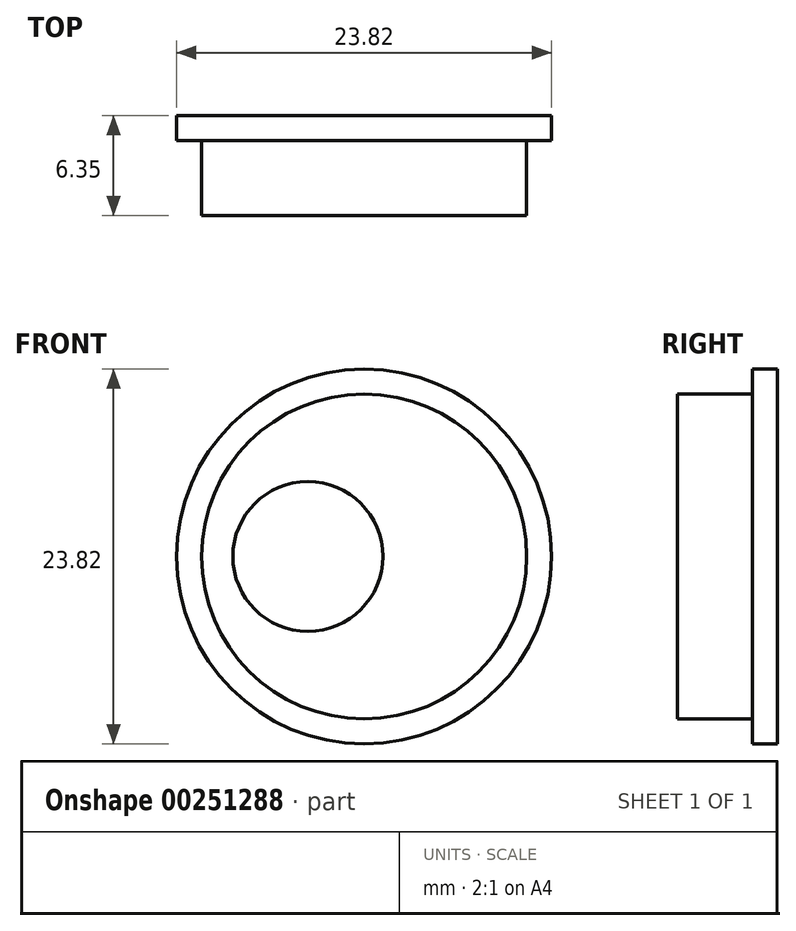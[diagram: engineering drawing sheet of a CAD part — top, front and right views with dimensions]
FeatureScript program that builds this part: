
annotation { "Feature Type Name" : "Feature", "Feature Type Description" : "" }
export const myFeature = defineFeature(function(context is Context, id is Id, definition is map)
    precondition{}
    {
        {
            var Q0;
            Q0=qCreatedBy(makeId("Front.planeOp"),FACE);
            var sketch = newSketch(context, id + "F0", { "sketchPlane" : qUnion([Q0])});
            skCircle(sketch, "E0", {"center": v(0, 0) * mm, "radius": 11.9 * mm});
            skSolve(sketch);
        }
        {
            var Q0;
            Q0 = qSketchRegion(id + "F0", true);
            extrude(context, id + "F1", {"entities" : qUnion([Q0]), "depth" : 1.59 * mm});
        }
        {
            var Q0;
            Q0=makeQuery(id+"F1.opExtrude","CAP_FACE",FACE,{"disambiguationData":[OSD([sQuery(id+"F0.wireOp",EDGE,"E0")])],"isStart":false});
            var sketch = newSketch(context, id + "F2", { "sketchPlane" : qUnion([Q0])});
            skCircle(sketch, "E1", {"center": v(0, 0) * mm, "radius": 10.32 * mm});
            skSolve(sketch);
        }
        {
            var Q0;
            Q0 = qSketchRegion(id + "F2", true);
            extrude(context, id + "F3", {"entities" : qUnion([Q0]), "operationType" : NewBodyOperationType.ADD, "depth" : 4.76 * mm});
        }
        {
            var Q0;
            Q0=makeQuery(id+"F3.opExtrude","CAP_FACE",FACE,{"disambiguationData":[OSD([sQuery(id+"F2.wireOp",EDGE,"E1")])],"isStart":false});
            var sketch = newSketch(context, id + "F4", { "sketchPlane" : qUnion([Q0])});
            skCircle(sketch, "E2", {"center": v(-3.57, 0) * mm, "radius": 4.76 * mm});
            skSolve(sketch);
        }
        {
            var Q0;
            Q0 = qSketchRegion(id + "F4", true);
            extrude(context, id + "F5", {"entities" : qUnion([Q0]), "operationType" : NewBodyOperationType.ADD, "depth" : 1 / 203.2 * mm});
        }
    });
